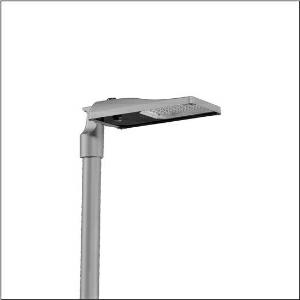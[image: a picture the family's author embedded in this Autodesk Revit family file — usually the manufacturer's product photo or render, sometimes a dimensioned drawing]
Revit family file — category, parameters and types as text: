
# Revit family: streetlight_sl_31_mini___st0_8a_5xh6c31t08ha_0974
name_source: partatom
category: Lighting Fixtures
units: mm (PartAtom-declared; Revit-internal decimal feet)

## family parameters
Cut with Voids When Loaded = No
Host = Face
Light Source = No
Part Type = Normal
Room Calculation Point = No
Round Connector Dimension = Use Diameter
Shared = No

## types (1)
- --- (1 x LED, 9230 lm, 68.3 W, 3000K)
    Apparent Load = 68 VA
    CIE Flux Codes = 38 75 97 100 100
    Color Rendering = 70
    Color Temperature = 3000K
    Default Elevation = 1800 mm
    Description = Streetlight SL 31 mini D4i, Desk-Remote mast luminaire for post-top, side-entry; light control with lens of PMMA; light distribution: ST0.8a, direct asymmetric distribution, for standard-compliant lighting for roads and squares; LED: luminous flux: 9.230lm, light colour: 730, colour temperature: 3000K; luminous efficacy: 135,1lm/W; control: pre-setting: logarithmic dimming characteristic, flexible luminous flux parameterisation, time-dependent luminous flux control, constant luminous flux control, power reduction, intelligent temperature release in ECG and LED module, overheat protection; luminaire housing, of diecast aluminium, SITECO metallic grey (DB 702S), corrosivity category C5 high according to DIN EN ISO 12944; cover of toughened safety glass, transparent, opened without tools; mast flange of diecast aluminium, SITECO metallic grey (DB 702S), spigot size: 76/60mm, mast flange included unmounted; with cable H07RN-F 2x 1.5mm², cable length: 8,5m, connection cable pre-assembled; mains connection: 220..240V, AC, 50/60Hz; power consumption (at start of service life): 68,3W / (at end of service life): 74,5W / (with reduced operation 50%): 29,5W; protection rating (complete): IP66; insulation class (complete): insulation class II (safety insulation); impact resistance: IK09; certification: CE, ENEC, ENEC+, VDE, UKCA, ZD4i; permissible operating ambient temperature for outdoor applications: -40..+50°C; packaging unit: 1 piece

Light Distribution: ST0.8a
    Height = 76 mm
    Lamp = 1 x LED
    Lamp Light Flux = 9230 lm
    Lamp Power = 68.3 W
    Lamp count = 1
    Length = 547 mm
    Luminous efficacy = 135 lm/W
    Manufacturer = Siteco
    ModVariant = No
    Model = 5XH6C31T08HA
    Number of Poles = 1
    OnlyDefault = Yes
    Power Factor = 1
    Product Name = Streetlight SL 31 mini | ST0.8a
    Product group = mast luminaire | pylon top
    ProductGroupID = 6100
    Protection Class = Protection class II
    Protection Degree = IP 66
    RLX_Detail_Level = 1
    RLX_Emergency_Light_Flux = 0 lm
    RLX_Emergency_Type = 0
    RLX_Emergency_Type_DB = No
    RlxData = <blob elided: 24361 chars, md5=339053b2>
    Socket = socket
    Standby Power = 0 W
    System Light Flux = 9230 lm
    System Power = 68 W
    Type Comments = factory setting: luminous flux: 100 % | dim-lin: 254 | 692 mA
    Type Image = l_1300332.jpg
    URL = http://relux.com
    VarID = @adj_020093
    Voltage = 0 V
    Weight = 0.00 kg
    Width = 265 mm

## geometry (parser evidence)
native form markers: Blend x4, Sweep x10
no freeform markers — native parametric forms only
